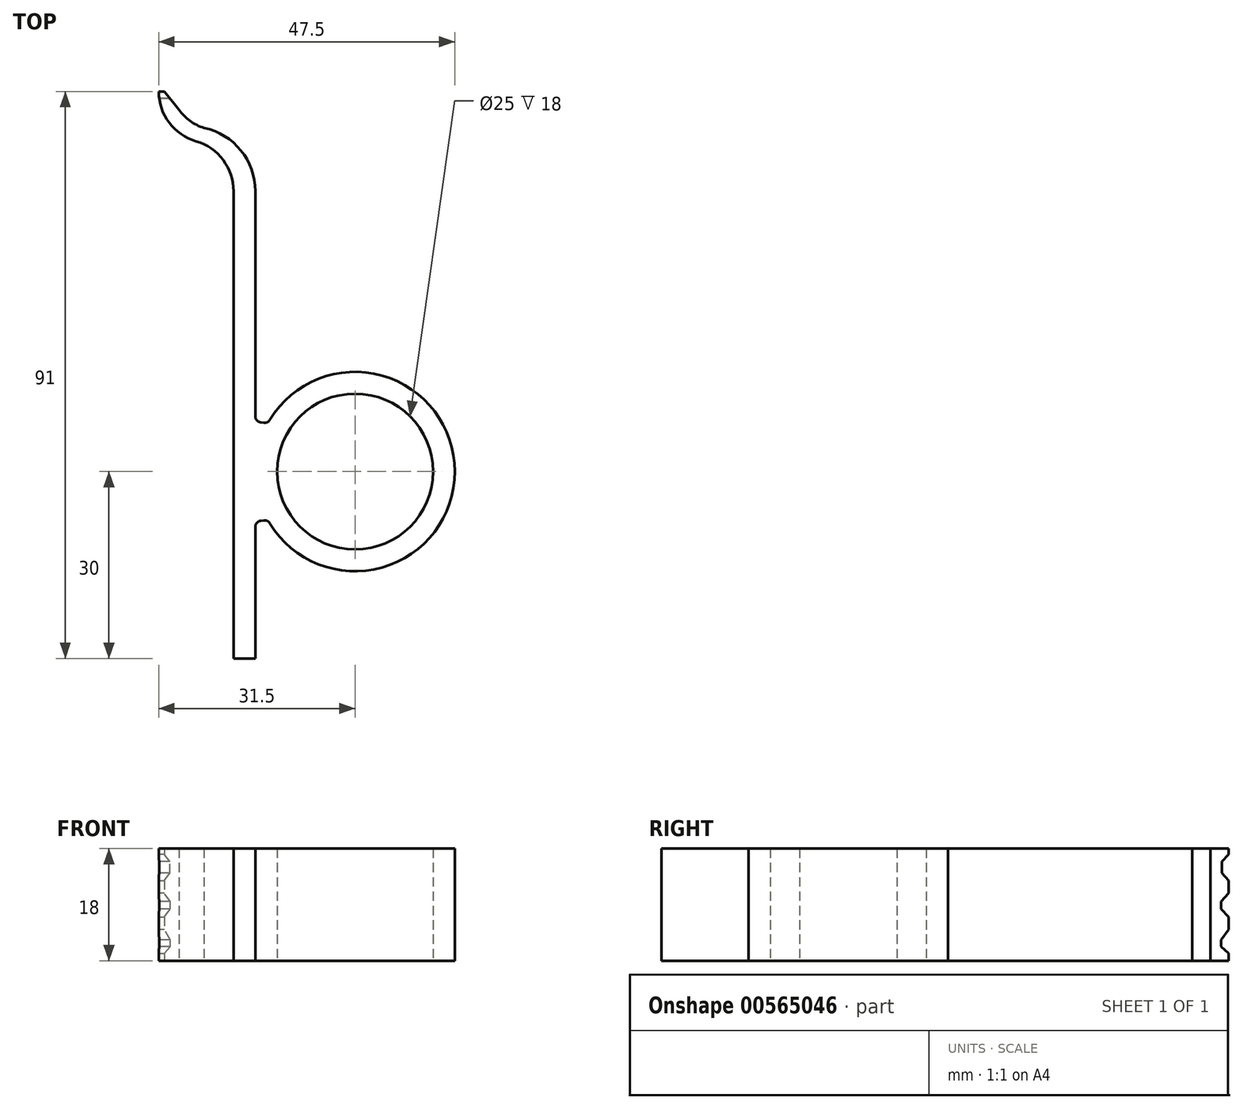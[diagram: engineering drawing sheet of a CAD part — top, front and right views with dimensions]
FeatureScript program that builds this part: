
annotation { "Feature Type Name" : "Feature", "Feature Type Description" : "" }
export const myFeature = defineFeature(function(context is Context, id is Id, definition is map)
    precondition{}
    {
        {
            var Q0;
            Q0=qCreatedBy(makeId("Top.planeOp"),FACE);
            var sketch = newSketch(context, id + "F0", { "sketchPlane" : qUnion([Q0])});
            skCircle(sketch, "E0", {"center": v(0, 0) * mm, "radius": 12.5 * mm});
            skCircle(sketch, "E1", {"center": v(0, 0) * mm, "radius": 16 * mm});
            skLineSegment(sketch, "E2.bottom", {"start": v(-16, 45) * mm, "end": v(-19.5, 45) * mm});
            skLineSegment(sketch, "E2.top", {"start": v(-16, -30) * mm, "end": v(-19.5, -30) * mm});
            skLineSegment(sketch, "E2.left", {"start": v(-16, 45) * mm, "end": v(-16, -30) * mm});
            skLineSegment(sketch, "E2.right", {"start": v(-19.5, 45) * mm, "end": v(-19.5, -30) * mm});
            skLineSegment(sketch, "E3.bottom", {"start": v(-16, -30) * mm, "end": v(0, -30) * mm, "construction": true});
            skLineSegment(sketch, "E3.top", {"start": v(-16, 0) * mm, "end": v(0, 0) * mm, "construction": true});
            skLineSegment(sketch, "E3.left", {"start": v(-16, -30) * mm, "end": v(-16, 0) * mm, "construction": true});
            skLineSegment(sketch, "E3.right", {"start": v(0, -30) * mm, "end": v(0, 0) * mm, "construction": true});
            skLineSegment(sketch, "E4", {"start": v(-16, 0) * mm, "end": v(-16, 8) * mm, "construction": true});
            skLineSegment(sketch, "E5", {"start": v(-16, 0) * mm, "end": v(-16, -8) * mm, "construction": true});
            skLineSegment(sketch, "E6", {"start": v(-16, 0) * mm, "end": v(-14, 7.75) * mm});
            skLineSegment(sketch, "E7", {"start": v(-16, 0) * mm, "end": v(-14, -7.75) * mm});
            skLineSegment(sketch, "E8", {"start": v(-16, 8) * mm, "end": v(-14, 7.75) * mm});
            skLineSegment(sketch, "E9", {"start": v(-16, -8) * mm, "end": v(-14, -7.75) * mm});
            skLineSegment(sketch, "E10.bottom", {"start": v(-19.5, 45) * mm, "end": v(-16, 45) * mm});
            skLineSegment(sketch, "E10.top", {"start": v(-19.5, 61) * mm, "end": v(-16, 61) * mm});
            skLineSegment(sketch, "E10.left", {"start": v(-19.5, 45) * mm, "end": v(-19.5, 61) * mm});
            skLineSegment(sketch, "E10.right", {"start": v(-16, 45) * mm, "end": v(-16, 61) * mm});
            skLineSegment(sketch, "E11.bottom", {"start": v(-19.5, 61) * mm, "end": v(-31.5, 61) * mm});
            skLineSegment(sketch, "E11.top", {"start": v(-19.5, 45) * mm, "end": v(-31.5, 45) * mm});
            skLineSegment(sketch, "E11.left", {"start": v(-19.5, 61) * mm, "end": v(-19.5, 45) * mm});
            skLineSegment(sketch, "E11.right", {"start": v(-31.5, 61) * mm, "end": v(-31.5, 45) * mm});
            skLineSegment(sketch, "E12.bottom", {"start": v(-31.5, 61) * mm, "end": v(-19.5, 61) * mm});
            skLineSegment(sketch, "E12.top", {"start": v(-31.5, 53) * mm, "end": v(-19.5, 53) * mm});
            skLineSegment(sketch, "E12.left", {"start": v(-31.5, 61) * mm, "end": v(-31.5, 53) * mm});
            skLineSegment(sketch, "E12.right", {"start": v(-19.5, 61) * mm, "end": v(-19.5, 53) * mm});
            skLineSegment(sketch, "E13", {"start": v(-31.5, 53) * mm, "end": v(-25.5, 53) * mm});
            skArc(sketch, "E14", {"start": v(-31.5, 61) * mm, "mid": v(-29.83, 56) * mm, "end": v(-25.5, 53) * mm});
            skArc(sketch, "E15", {"start": v(-19.5, 45) * mm, "mid": v(-21.17, 50) * mm, "end": v(-25.5, 53) * mm});
            skLineSegment(sketch, "E16", {"start": v(-31.5, 61) * mm, "end": v(-29.5, 61) * mm});
            skLineSegment(sketch, "E17", {"start": v(-25.5, 53) * mm, "end": v(-24.22, 55.15) * mm});
            skArc(sketch, "E18", {"start": v(-29.5, 61) * mm, "mid": v(-27.67, 57.35) * mm, "end": v(-24.22, 55.15) * mm});
            skArc(sketch, "E19", {"start": v(-16, 45) * mm, "mid": v(-18.31, 51.53) * mm, "end": v(-24.22, 55.15) * mm});
            skSolve(sketch);
        }
        {
            var Q0;
            {var subQ3=sQuery(id+"F0.wireOp",EDGE,"E2.bottom");Q0=makeQuery(id+"F0.imprint","IMPRINT",FACE,{"disambiguationData":[TD([[makeQuery(id+"F0.imprint","IMPRINT",EDGE,{"derivedFrom":subQ3}),1.0]])]});}
            var Q1;
            Q1=makeQuery(id+"F0.imprint","IMPRINT",FACE,{"disambiguationData":[TD([[makeQuery(id+"F0.imprint","IMPRINT",EDGE,{"derivedFrom":sQuery(id+"F0.wireOp",EDGE,"E0")}),-1.0]])]});
            var Q2;
            {var subQ4=sQuery(id+"F0.wireOp",EDGE,"E9");Q2=makeQuery(id+"F0.imprint","IMPRINT",FACE,{"disambiguationData":[TD([[makeQuery(id+"F0.imprint","IMPRINT",EDGE,{"derivedFrom":subQ4}),1.0]])]});}
            var Q3;
            {var subQ0=sQuery(id+"F0.wireOp",EDGE,"E7");Q3=makeQuery(id+"F0.imprint","IMPRINT",FACE,{"disambiguationData":[TD([[makeQuery(id+"F0.imprint","IMPRINT",EDGE,{"derivedFrom":subQ0}),-1.0]])]});}
            var Q4;
            {var subQ4=sQuery(id+"F0.wireOp",EDGE,"E8");Q4=makeQuery(id+"F0.imprint","IMPRINT",FACE,{"disambiguationData":[TD([[makeQuery(id+"F0.imprint","IMPRINT",EDGE,{"derivedFrom":subQ4}),-1.0]])]});}
            var Q5;
            {var subQ0=sQuery(id+"F0.wireOp",EDGE,"E6");Q5=makeQuery(id+"F0.imprint","IMPRINT",FACE,{"disambiguationData":[TD([[makeQuery(id+"F0.imprint","IMPRINT",EDGE,{"derivedFrom":subQ0}),1.0]])]});}
            var Q6;
            {var subQ3=sQuery(id+"F0.wireOp",EDGE,"E2.bottom");Q6=makeQuery(id+"F0.imprint","IMPRINT",FACE,{"disambiguationData":[TD([[makeQuery(id+"F0.imprint","IMPRINT",EDGE,{"derivedFrom":subQ3}),1.0]])]});}
            var Q7;
            {var subQ0=sQuery(id+"F0.wireOp",EDGE,"E14");Q7=makeQuery(id+"F0.imprint","IMPRINT",FACE,{"disambiguationData":[TD([[makeQuery(id+"F0.imprint","IMPRINT",EDGE,{"derivedFrom":subQ0}),1.0]])]});}
            var Q8;
            {var subQ0=sQuery(id+"F0.wireOp",EDGE,"E15");Q8=makeQuery(id+"F0.imprint","IMPRINT",FACE,{"disambiguationData":[TD([[makeQuery(id+"F0.imprint","IMPRINT",EDGE,{"derivedFrom":subQ0}),-1.0]])]});}
            var Q9;
            {var subQ0=sQuery(id+"F0.wireOp",EDGE,"E2.bottom");Q9=makeQuery(id+"F0.imprint","IMPRINT",FACE,{"disambiguationData":[TD([[makeQuery(id+"F0.imprint","IMPRINT",EDGE,{"derivedFrom":subQ0}),-1.0]])]});}
            var Q10;
            {var subQ0=sQuery(id+"F0.wireOp",EDGE,"E17");Q10=makeQuery(id+"F0.imprint","IMPRINT",FACE,{"disambiguationData":[TD([[makeQuery(id+"F0.imprint","IMPRINT",EDGE,{"derivedFrom":subQ0}),-1.0]])]});}
            extrude(context, id + "F1", {"entities" : qUnion([Q0, Q1, Q2, Q3, Q4, Q5, Q6, Q7, Q8, Q9, Q10]), "depth" : 18 * mm, "offsetDistance" : 25 * mm});
        }
        {
            var Q0;
            Q0=makeQuery(id+"F1.opExtrude","SWEPT_EDGE",EDGE,{"disambiguationData":[OSD([sQuery(id+"F0.wireOp",EDGE,"E2.left"),sQuery(id+"F0.wireOp",EDGE,"E9")])]});
            var Q1;
            Q1=makeQuery(id+"F1.opExtrude","SWEPT_EDGE",EDGE,{"disambiguationData":[OSD([sQuery(id+"F0.wireOp",EDGE,"E1"),sQuery(id+"F0.wireOp",EDGE,"E7"),sQuery(id+"F0.wireOp",EDGE,"E9")])]});
            var Q2;
            Q2=makeQuery(id+"F1.opExtrude","SWEPT_EDGE",EDGE,{"disambiguationData":[OSD([sQuery(id+"F0.wireOp",EDGE,"E1"),sQuery(id+"F0.wireOp",EDGE,"E6"),sQuery(id+"F0.wireOp",EDGE,"E8")])]});
            var Q3;
            Q3=makeQuery(id+"F1.opExtrude","SWEPT_EDGE",EDGE,{"disambiguationData":[OSD([sQuery(id+"F0.wireOp",EDGE,"E2.left"),sQuery(id+"F0.wireOp",EDGE,"E8")])]});
            fillet(context, id + "F2", {"entities" : qUnion([Q0, Q1, Q2, Q3]), "radius" : 1 * mm, "tangentPropagation" : true, "allowEdgeOverflow" : false});
        }
        {
            var Q0;
            Q0=makeQuery(id+"F1.opExtrude","SWEPT_EDGE",EDGE,{"disambiguationData":[OSD([sQuery(id+"F0.wireOp",EDGE,"E11.bottom"),sQuery(id+"F0.wireOp",EDGE,"E18")])]});
            chamfer(context, id + "F3", {"entities" : qUnion([Q0]), "chamferType" : ChamferType.OFFSET_ANGLE, "width" : 2 * mm, "oppositeDirection" : false, "angle" : 55 * degree, "tangentPropagation" : true});
        }
        {
            var Q0;
            Q0=makeQuery(id+"F1.opExtrude","SWEPT_FACE",FACE,{"disambiguationData":[OSD([sQuery(id+"F0.wireOp",EDGE,"E2.right")])]});
            cPlane(context, id + "F4", {"entities" : qUnion([Q0]), "cplaneType" : CPlaneType.OFFSET, "offset" : 15 * mm, "width" : 150 * mm, "height" : 150 * mm});
        }
        {
            var Q0;
            Q0=qCreatedBy(id+"F4.planeOp",FACE);
            var sketch = newSketch(context, id + "F5", { "sketchPlane" : qUnion([Q0])});
            skLineSegment(sketch, "E20.bottom", {"start": v(-46.77, 18.03) * mm, "end": v(-61.01, 18.03) * mm});
            skLineSegment(sketch, "E20.top", {"start": v(-46.77, 0) * mm, "end": v(-61.01, 0) * mm});
            skLineSegment(sketch, "E20.left", {"start": v(-46.77, 18.03) * mm, "end": v(-46.77, 0) * mm});
            skLineSegment(sketch, "E21", {"start": v(-61.01, 18.03) * mm, "end": v(-61.01, 0) * mm});
            skLineSegment(sketch, "E22", {"start": v(-61.62, 1.02) * mm, "end": v(-61.2, 1.02) * mm});
            skLineSegment(sketch, "E23", {"start": v(-61.2, 1.02) * mm, "end": v(-59.83, 2.23) * mm});
            skLineSegment(sketch, "E24", {"start": v(-59.83, 2.23) * mm, "end": v(-59.83, 3.36) * mm});
            skLineSegment(sketch, "E25", {"start": v(-59.83, 3.36) * mm, "end": v(-61.4, 5.56) * mm});
            skLineSegment(sketch, "E26", {"start": v(-61.4, 5.56) * mm, "end": v(-61.4, 6.62) * mm});
            skLineSegment(sketch, "E27", {"start": v(-61.4, 6.62) * mm, "end": v(-59.82, 8.3) * mm});
            skLineSegment(sketch, "E28", {"start": v(-59.82, 8.3) * mm, "end": v(-59.82, 9.49) * mm});
            skLineSegment(sketch, "E29", {"start": v(-59.82, 9.49) * mm, "end": v(-61.3, 11.14) * mm});
            skLineSegment(sketch, "E30", {"start": v(-61.3, 11.14) * mm, "end": v(-61.3, 12.54) * mm});
            skLineSegment(sketch, "E31", {"start": v(-61.3, 12.54) * mm, "end": v(-59.91, 14.06) * mm});
            skLineSegment(sketch, "E32", {"start": v(-59.91, 14.06) * mm, "end": v(-59.91, 15.92) * mm});
            skLineSegment(sketch, "E33", {"start": v(-59.91, 15.92) * mm, "end": v(-61.32, 17.36) * mm});
            skLineSegment(sketch, "E34", {"start": v(-61.32, 17.36) * mm, "end": v(-62.24, 15.45) * mm});
            skLineSegment(sketch, "E35", {"start": v(-62.24, 15.45) * mm, "end": v(-62.38, 1.02) * mm});
            skLineSegment(sketch, "E36", {"start": v(-62.38, 1.02) * mm, "end": v(-61.62, 1.02) * mm});
            skSolve(sketch);
        }
        {
            var Q0;
            {var subQ3=sQuery(id+"F5.wireOp",EDGE,"E22");Q0=makeQuery(id+"F5.imprint","IMPRINT",FACE,{"disambiguationData":[TD([[makeQuery(id+"F5.imprint","IMPRINT",EDGE,{"derivedFrom":subQ3}),1.0]])]});}
            var Q1;
            {var subQ5=sQuery(id+"F5.wireOp",EDGE,"E24");Q1=makeQuery(id+"F5.imprint","IMPRINT",FACE,{"disambiguationData":[TD([[makeQuery(id+"F5.imprint","IMPRINT",EDGE,{"derivedFrom":subQ5}),1.0]])]});}
            var Q2;
            {var subQ5=sQuery(id+"F5.wireOp",EDGE,"E28");Q2=makeQuery(id+"F5.imprint","IMPRINT",FACE,{"disambiguationData":[TD([[makeQuery(id+"F5.imprint","IMPRINT",EDGE,{"derivedFrom":subQ5}),1.0]])]});}
            var Q3;
            {var subQ5=sQuery(id+"F5.wireOp",EDGE,"E32");Q3=makeQuery(id+"F5.imprint","IMPRINT",FACE,{"disambiguationData":[TD([[makeQuery(id+"F5.imprint","IMPRINT",EDGE,{"derivedFrom":subQ5}),1.0]])]});}
            extrude(context, id + "F6", {"entities" : qUnion([Q0, Q1, Q2, Q3]), "operationType" : NewBodyOperationType.REMOVE, "oppositeDirection" : true, "depth" : 25 * mm, "offsetDistance" : 25 * mm});
        }
    });
